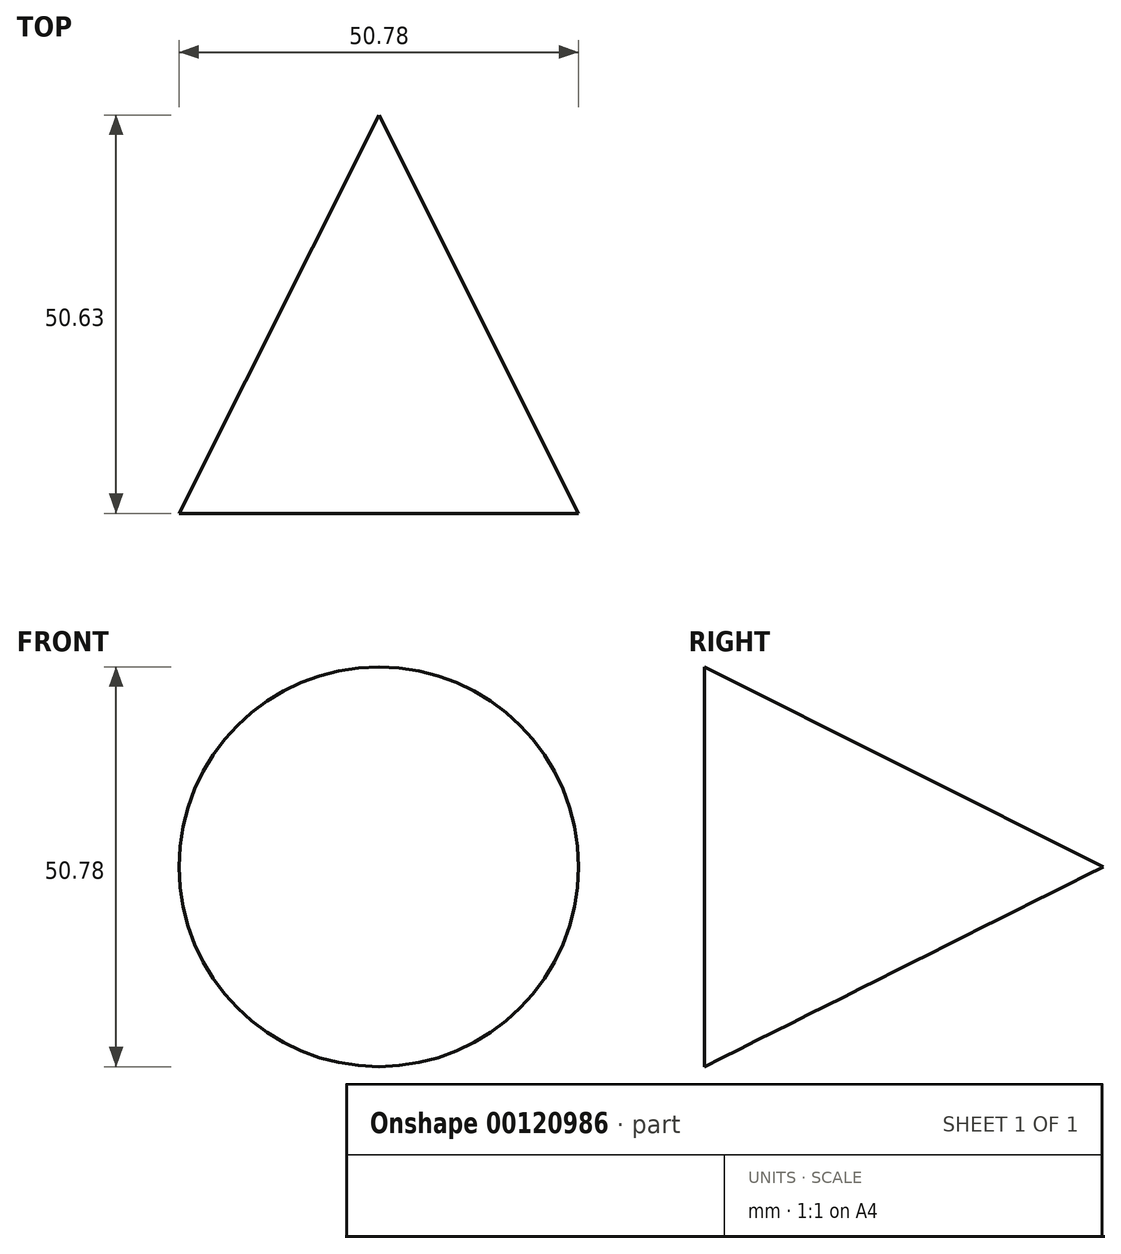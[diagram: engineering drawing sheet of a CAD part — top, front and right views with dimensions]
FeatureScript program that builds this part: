
annotation { "Feature Type Name" : "Feature", "Feature Type Description" : "" }
export const myFeature = defineFeature(function(context is Context, id is Id, definition is map)
    precondition{}
    {
        {
            var Q0;
            Q0=qCreatedBy(makeId("Top.planeOp"),FACE);
            var sketch = newSketch(context, id + "F0", { "sketchPlane" : qUnion([Q0])});
            skLineSegment(sketch, "E0", {"start": v(0, 0) * mm, "end": v(0, 50.63) * mm});
            skLineSegment(sketch, "E1", {"start": v(0, 50.63) * mm, "end": v(25.39, 0) * mm});
            skLineSegment(sketch, "E2", {"start": v(25.39, 0) * mm, "end": v(0, 0) * mm});
            skSolve(sketch);
        }
        {
            var Q0;
            Q0=makeQuery(id+"F0.imprint","IMPRINT",FACE,{"disambiguationData":[TD([[makeQuery(id+"F0.imprint","IMPRINT",EDGE,{"derivedFrom":sQuery(id+"F0.wireOp",EDGE,"E0")}),-1.0]])]});
            var Q1;
            Q1=sQuery(id+"F0.wireOp",EDGE,"E0");
            revolve(context, id + "F1", {"entities" : qUnion([Q0]), "axis" : qUnion([Q1]), "revolveType" : RevolveType.FULL});
        }
    });
